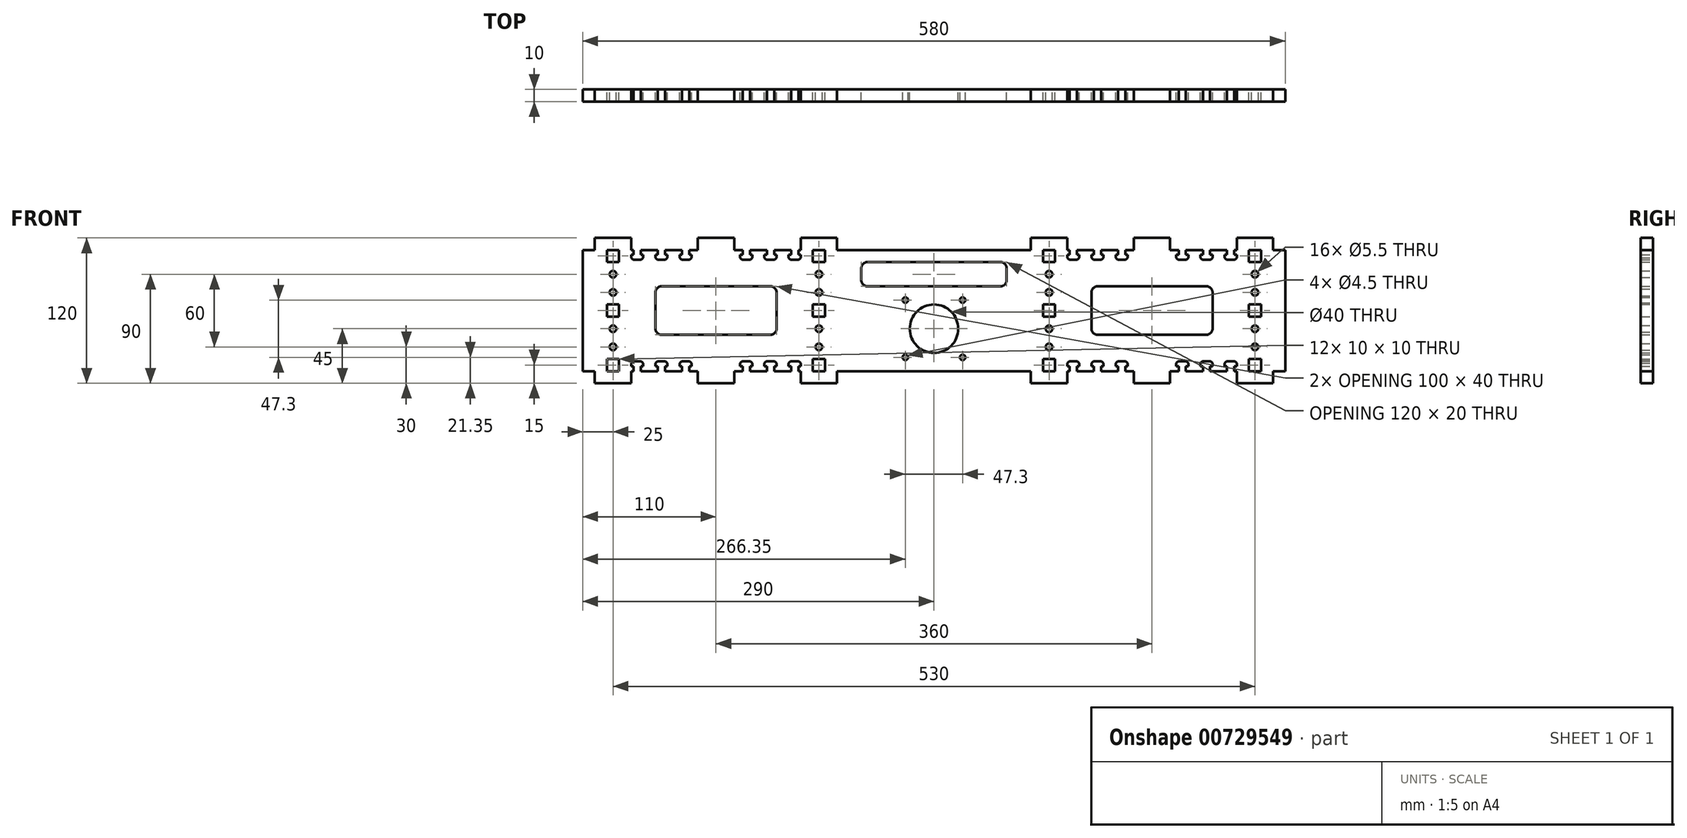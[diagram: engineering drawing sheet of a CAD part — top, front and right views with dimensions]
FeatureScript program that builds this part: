
annotation { "Feature Type Name" : "Feature", "Feature Type Description" : "" }
export const myFeature = defineFeature(function(context is Context, id is Id, definition is map)
    precondition{}
    {
        {
            var Q0;
            Q0=qCreatedBy(makeId("Front.planeOp"),FACE);
            var sketch = newSketch(context, id + "F0", { "sketchPlane" : qUnion([Q0])});
            skLineSegment(sketch, "E0.bottom", {"start": v(0, -50) * mm, "end": v(-290, -50) * mm, "construction": true});
            skLineSegment(sketch, "E0.top", {"start": v(0, 50) * mm, "end": v(-165, 50) * mm, "construction": true});
            skLineSegment(sketch, "E0.right", {"start": v(-290, -50) * mm, "end": v(-290, 50) * mm});
            skLineSegment(sketch, "E1", {"start": v(0, -50) * mm, "end": v(0, 83) * mm, "construction": true});
            skLineSegment(sketch, "E2", {"start": v(-265, 50) * mm, "end": v(-265, -50) * mm, "construction": true});
            skPoint(sketch, "E3.middle", {"position": v(-265, 0) * mm});
            skLineSegment(sketch, "E4.bottom", {"start": v(-260, 40) * mm, "end": v(-270, 40) * mm});
            skLineSegment(sketch, "E4.top", {"start": v(-260, 50) * mm, "end": v(-270, 50) * mm});
            skLineSegment(sketch, "E4.left", {"start": v(-260, 40) * mm, "end": v(-260, 50) * mm});
            skLineSegment(sketch, "E4.right", {"start": v(-270, 40) * mm, "end": v(-270, 50) * mm});
            skPoint(sketch, "E4.middle", {"position": v(-265, 45) * mm});
            skLineSegment(sketch, "E5", {"start": v(0, 0) * mm, "end": v(-290, 0) * mm, "construction": true});
            skLineSegment(sketch, "E6.bottom", {"start": v(-260, 5) * mm, "end": v(-270, 5) * mm});
            skLineSegment(sketch, "E6.top", {"start": v(-260, -5) * mm, "end": v(-270, -5) * mm});
            skLineSegment(sketch, "E6.left", {"start": v(-260, 5) * mm, "end": v(-260, -5) * mm});
            skLineSegment(sketch, "E6.right", {"start": v(-270, 5) * mm, "end": v(-270, -5) * mm});
            skLineSegment(sketch, "E7", {"start": v(-180, 63.21) * mm, "end": v(-180, -50) * mm, "construction": true});
            skLineSegment(sketch, "E8.bottom", {"start": v(-195, 60) * mm, "end": v(-180, 60) * mm});
            skLineSegment(sketch, "E8.left", {"start": v(-195, 60) * mm, "end": v(-195, 50) * mm});
            skPoint(sketch, "E8.middle", {"position": v(-180, 50) * mm});
            skLineSegment(sketch, "E9.trimOffspring", {"start": v(-195, 50) * mm, "end": v(-290, 50) * mm, "construction": true});
            skLineSegment(sketch, "E10.MirrorCS", {"start": v(-165, 60) * mm, "end": v(-180, 60) * mm});
            skLineSegment(sketch, "E11.MirrorCS", {"start": v(-165, 60) * mm, "end": v(-165, 50) * mm});
            skLineSegment(sketch, "E12.MirrorCS", {"start": v(-260, -40) * mm, "end": v(-260, -50) * mm});
            skLineSegment(sketch, "E13.MirrorCS", {"start": v(-260, -50) * mm, "end": v(-270, -50) * mm});
            skLineSegment(sketch, "E14.MirrorCS", {"start": v(-270, -40) * mm, "end": v(-270, -50) * mm});
            skLineSegment(sketch, "E15.MirrorCS", {"start": v(-260, -40) * mm, "end": v(-270, -40) * mm});
            skLineSegment(sketch, "E16.MirrorCS", {"start": v(-100, 40) * mm, "end": v(-100, 50) * mm});
            skLineSegment(sketch, "E17.MirrorCS", {"start": v(-100, 50) * mm, "end": v(-90, 50) * mm});
            skLineSegment(sketch, "E18.MirrorCS", {"start": v(-90, 40) * mm, "end": v(-90, 50) * mm});
            skLineSegment(sketch, "E19.MirrorCS", {"start": v(-100, 40) * mm, "end": v(-90, 40) * mm});
            skLineSegment(sketch, "E20.MirrorCS", {"start": v(-100, 5) * mm, "end": v(-90, 5) * mm});
            skLineSegment(sketch, "E21.MirrorCS", {"start": v(-100, 5) * mm, "end": v(-100, -5) * mm});
            skLineSegment(sketch, "E22.MirrorCS", {"start": v(-90, 5) * mm, "end": v(-90, -5) * mm});
            skLineSegment(sketch, "E23.MirrorCS", {"start": v(-100, -5) * mm, "end": v(-90, -5) * mm});
            skLineSegment(sketch, "E24.MirrorCS", {"start": v(-195, -60) * mm, "end": v(-195, -50) * mm});
            skLineSegment(sketch, "E25.MirrorCS", {"start": v(-195, -60) * mm, "end": v(-180, -60) * mm});
            skLineSegment(sketch, "E26.MirrorCS", {"start": v(-165, -60) * mm, "end": v(-180, -60) * mm});
            skLineSegment(sketch, "E27.MirrorCS", {"start": v(-165, -60) * mm, "end": v(-165, -50) * mm});
            skLineSegment(sketch, "E28.MirrorCS", {"start": v(0, -50) * mm, "end": v(-165, -50) * mm, "construction": true});
            skLineSegment(sketch, "E29.MirrorCS", {"start": v(-90, -40) * mm, "end": v(-90, -50) * mm});
            skLineSegment(sketch, "E30.MirrorCS", {"start": v(-100, -40) * mm, "end": v(-90, -40) * mm});
            skLineSegment(sketch, "E31.MirrorCS", {"start": v(-100, -50) * mm, "end": v(-90, -50) * mm});
            skLineSegment(sketch, "E32.MirrorCS", {"start": v(-100, -40) * mm, "end": v(-100, -50) * mm});
            skLineSegment(sketch, "E33", {"start": v(-290, 50) * mm, "end": v(-280, 50) * mm});
            skLineSegment(sketch, "E34", {"start": v(-280, 50) * mm, "end": v(-280, 60) * mm});
            skLineSegment(sketch, "E35", {"start": v(-280, 60) * mm, "end": v(-250, 60) * mm});
            skLineSegment(sketch, "E36", {"start": v(-250, 60) * mm, "end": v(-250, 50) * mm});
            skLineSegment(sketch, "E37.MirrorCS", {"start": v(-250, -60) * mm, "end": v(-250, -50) * mm});
            skLineSegment(sketch, "E38.MirrorCS", {"start": v(-280, -60) * mm, "end": v(-250, -60) * mm});
            skLineSegment(sketch, "E39.MirrorCS", {"start": v(-290, -50) * mm, "end": v(-280, -50) * mm});
            skLineSegment(sketch, "E40.MirrorCS", {"start": v(-280, -50) * mm, "end": v(-280, -60) * mm});
            skLineSegment(sketch, "E41.MirrorCS", {"start": v(-195, -50) * mm, "end": v(-290, -50) * mm, "construction": true});
            skLineSegment(sketch, "E42", {"start": v(-205, 42) * mm, "end": v(-205, 50) * mm, "construction": true});
            skLineSegment(sketch, "E43", {"start": v(-205, 42) * mm, "end": v(-201.6, 42) * mm});
            skLineSegment(sketch, "E44", {"start": v(-201.6, 42) * mm, "end": v(-200, 43.6) * mm});
            skLineSegment(sketch, "E45", {"start": v(-200, 43.6) * mm, "end": v(-200, 46) * mm});
            skLineSegment(sketch, "E46", {"start": v(-200, 46) * mm, "end": v(-202, 46) * mm});
            skLineSegment(sketch, "E47", {"start": v(-202, 46) * mm, "end": v(-202, 50) * mm});
            skLineSegment(sketch, "E48", {"start": v(-202, 50) * mm, "end": v(-208, 50) * mm, "construction": true});
            skLineSegment(sketch, "E49", {"start": v(-207.5, 42) * mm, "end": v(-207.5, 50) * mm, "construction": true});
            skLineSegment(sketch, "E50.MirrorCS", {"start": v(-205, 42) * mm, "end": v(-208.4, 42) * mm});
            skLineSegment(sketch, "E51.MirrorCS", {"start": v(-202.5, 42) * mm, "end": v(-202.5, 50) * mm, "construction": true});
            skLineSegment(sketch, "E52.MirrorCS", {"start": v(-208, 50) * mm, "end": v(-202, 50) * mm, "construction": true});
            skLineSegment(sketch, "E53.MirrorCS", {"start": v(-208, 46) * mm, "end": v(-208, 50) * mm});
            skLineSegment(sketch, "E54.MirrorCS", {"start": v(-210, 46) * mm, "end": v(-208, 46) * mm});
            skLineSegment(sketch, "E55.MirrorCS", {"start": v(-210, 43.6) * mm, "end": v(-210, 46) * mm});
            skLineSegment(sketch, "E56.MirrorCS", {"start": v(-208.4, 42) * mm, "end": v(-210, 43.6) * mm});
            skLineSegment(sketch, "E57.1.0.0", {"start": v(-221.6, 42) * mm, "end": v(-220, 43.6) * mm});
            skLineSegment(sketch, "E57.1.0.1", {"start": v(-220, 46) * mm, "end": v(-222, 46) * mm});
            skLineSegment(sketch, "E57.1.0.2", {"start": v(-225, 42) * mm, "end": v(-221.6, 42) * mm});
            skLineSegment(sketch, "E57.1.0.3", {"start": v(-228, 46) * mm, "end": v(-228, 50) * mm});
            skLineSegment(sketch, "E57.1.0.4", {"start": v(-230, 46) * mm, "end": v(-228, 46) * mm});
            skLineSegment(sketch, "E57.1.0.5", {"start": v(-225, 42) * mm, "end": v(-228.4, 42) * mm});
            skLineSegment(sketch, "E57.1.0.6", {"start": v(-230, 43.6) * mm, "end": v(-230, 46) * mm});
            skLineSegment(sketch, "E57.1.0.7", {"start": v(-220, 43.6) * mm, "end": v(-220, 46) * mm});
            skLineSegment(sketch, "E57.1.0.8", {"start": v(-228.4, 42) * mm, "end": v(-230, 43.6) * mm});
            skLineSegment(sketch, "E57.1.0.9", {"start": v(-222, 46) * mm, "end": v(-222, 50) * mm});
            skLineSegment(sketch, "E57.1.0.10", {"start": v(-222, 50) * mm, "end": v(-228, 50) * mm, "construction": true});
            skLineSegment(sketch, "E57.2.0.0", {"start": v(-241.6, 42) * mm, "end": v(-240, 43.6) * mm});
            skLineSegment(sketch, "E57.2.0.1", {"start": v(-240, 46) * mm, "end": v(-242, 46) * mm});
            skLineSegment(sketch, "E57.2.0.2", {"start": v(-245, 42) * mm, "end": v(-241.6, 42) * mm});
            skLineSegment(sketch, "E57.2.0.3", {"start": v(-248, 46) * mm, "end": v(-248, 50) * mm});
            skLineSegment(sketch, "E57.2.0.4", {"start": v(-250, 46) * mm, "end": v(-248, 46) * mm});
            skLineSegment(sketch, "E57.2.0.5", {"start": v(-245, 42) * mm, "end": v(-248.4, 42) * mm});
            skLineSegment(sketch, "E57.2.0.6", {"start": v(-250, 43.6) * mm, "end": v(-250, 46) * mm});
            skLineSegment(sketch, "E57.2.0.7", {"start": v(-240, 43.6) * mm, "end": v(-240, 46) * mm});
            skLineSegment(sketch, "E57.2.0.8", {"start": v(-248.4, 42) * mm, "end": v(-250, 43.6) * mm});
            skLineSegment(sketch, "E57.2.0.9", {"start": v(-242, 46) * mm, "end": v(-242, 50) * mm});
            skLineSegment(sketch, "E57.2.0.10", {"start": v(-242, 50) * mm, "end": v(-248, 50) * mm, "construction": true});
            skLineSegment(sketch, "E57.direction1", {"start": v(-208.4, 42) * mm, "end": v(-228.4, 42) * mm, "construction": true});
            skLineSegment(sketch, "E58", {"start": v(-250, 50) * mm, "end": v(-248, 50) * mm});
            skLineSegment(sketch, "E59", {"start": v(-242, 50) * mm, "end": v(-228, 50) * mm});
            skLineSegment(sketch, "E60", {"start": v(-222, 50) * mm, "end": v(-208, 50) * mm});
            skLineSegment(sketch, "E61", {"start": v(-195, 50) * mm, "end": v(-202, 50) * mm});
            skLineSegment(sketch, "E62.MirrorCS", {"start": v(-110, 50) * mm, "end": v(-112, 50) * mm});
            skLineSegment(sketch, "E63.MirrorCS", {"start": v(-152, 50) * mm, "end": v(-158, 50) * mm, "construction": true});
            skLineSegment(sketch, "E64.MirrorCS", {"start": v(-138, 50) * mm, "end": v(-132, 50) * mm, "construction": true});
            skLineSegment(sketch, "E65.MirrorCS", {"start": v(-165, 50) * mm, "end": v(-158, 50) * mm});
            skLineSegment(sketch, "E66.MirrorCS", {"start": v(-70, 50) * mm, "end": v(-80, 50) * mm});
            skLineSegment(sketch, "E67.MirrorCS", {"start": v(-158, 50) * mm, "end": v(-152, 50) * mm, "construction": true});
            skLineSegment(sketch, "E68.MirrorCS", {"start": v(-118, 50) * mm, "end": v(-112, 50) * mm, "construction": true});
            skLineSegment(sketch, "E69.MirrorCS", {"start": v(-118, 50) * mm, "end": v(-132, 50) * mm});
            skLineSegment(sketch, "E70.MirrorCS", {"start": v(-138, 50) * mm, "end": v(-152, 50) * mm});
            skLineSegment(sketch, "E71.MirrorCS", {"start": v(-80, 60) * mm, "end": v(-110, 60) * mm});
            skLineSegment(sketch, "E72.MirrorCS", {"start": v(-80, 50) * mm, "end": v(-80, 60) * mm});
            skLineSegment(sketch, "E73.MirrorCS", {"start": v(-110, 60) * mm, "end": v(-110, 50) * mm});
            skLineSegment(sketch, "E74.MirrorCS", {"start": v(-165, 50) * mm, "end": v(-70, 50) * mm, "construction": true});
            skLineSegment(sketch, "E75.MirrorCS", {"start": v(-155, 42) * mm, "end": v(-151.6, 42) * mm});
            skLineSegment(sketch, "E76.MirrorCS", {"start": v(-158, 46) * mm, "end": v(-158, 50) * mm});
            skLineSegment(sketch, "E77.MirrorCS", {"start": v(-158.4, 42) * mm, "end": v(-160, 43.6) * mm});
            skLineSegment(sketch, "E78.MirrorCS", {"start": v(-160, 46) * mm, "end": v(-158, 46) * mm});
            skLineSegment(sketch, "E79.MirrorCS", {"start": v(-131.6, 42) * mm, "end": v(-130, 43.6) * mm});
            skLineSegment(sketch, "E80.MirrorCS", {"start": v(-160, 43.6) * mm, "end": v(-160, 46) * mm});
            skLineSegment(sketch, "E81.MirrorCS", {"start": v(-112, 46) * mm, "end": v(-112, 50) * mm});
            skLineSegment(sketch, "E82.MirrorCS", {"start": v(-151.6, 42) * mm, "end": v(-150, 43.6) * mm});
            skLineSegment(sketch, "E83.MirrorCS", {"start": v(-155, 42) * mm, "end": v(-158.4, 42) * mm});
            skLineSegment(sketch, "E84.MirrorCS", {"start": v(-157.5, 42) * mm, "end": v(-157.5, 50) * mm, "construction": true});
            skLineSegment(sketch, "E85.MirrorCS", {"start": v(-110, 46) * mm, "end": v(-112, 46) * mm});
            skLineSegment(sketch, "E86.MirrorCS", {"start": v(-111.6, 42) * mm, "end": v(-110, 43.6) * mm});
            skLineSegment(sketch, "E87.MirrorCS", {"start": v(-132, 46) * mm, "end": v(-132, 50) * mm});
            skLineSegment(sketch, "E88.MirrorCS", {"start": v(-130, 43.6) * mm, "end": v(-130, 46) * mm});
            skLineSegment(sketch, "E89.MirrorCS", {"start": v(-140, 46) * mm, "end": v(-138, 46) * mm});
            skLineSegment(sketch, "E90.MirrorCS", {"start": v(-138.4, 42) * mm, "end": v(-140, 43.6) * mm});
            skLineSegment(sketch, "E91.MirrorCS", {"start": v(-152.5, 42) * mm, "end": v(-152.5, 50) * mm, "construction": true});
            skLineSegment(sketch, "E92.MirrorCS", {"start": v(-138, 46) * mm, "end": v(-138, 50) * mm});
            skLineSegment(sketch, "E93.MirrorCS", {"start": v(-118.4, 42) * mm, "end": v(-120, 43.6) * mm});
            skLineSegment(sketch, "E94.MirrorCS", {"start": v(-120, 43.6) * mm, "end": v(-120, 46) * mm});
            skLineSegment(sketch, "E95.MirrorCS", {"start": v(-150, 46) * mm, "end": v(-152, 46) * mm});
            skLineSegment(sketch, "E96.MirrorCS", {"start": v(-135, 42) * mm, "end": v(-138.4, 42) * mm});
            skLineSegment(sketch, "E97.MirrorCS", {"start": v(-150, 43.6) * mm, "end": v(-150, 46) * mm});
            skLineSegment(sketch, "E98.MirrorCS", {"start": v(-120, 46) * mm, "end": v(-118, 46) * mm});
            skLineSegment(sketch, "E99.MirrorCS", {"start": v(-115, 42) * mm, "end": v(-111.6, 42) * mm});
            skLineSegment(sketch, "E100.MirrorCS", {"start": v(-130, 46) * mm, "end": v(-132, 46) * mm});
            skLineSegment(sketch, "E101.MirrorCS", {"start": v(-118, 46) * mm, "end": v(-118, 50) * mm});
            skLineSegment(sketch, "E102.MirrorCS", {"start": v(-110, 43.6) * mm, "end": v(-110, 46) * mm});
            skLineSegment(sketch, "E103.MirrorCS", {"start": v(-115, 42) * mm, "end": v(-118.4, 42) * mm});
            skLineSegment(sketch, "E104.MirrorCS", {"start": v(-140, 43.6) * mm, "end": v(-140, 46) * mm});
            skLineSegment(sketch, "E105.MirrorCS", {"start": v(-152, 46) * mm, "end": v(-152, 50) * mm});
            skLineSegment(sketch, "E106.MirrorCS", {"start": v(-135, 42) * mm, "end": v(-131.6, 42) * mm});
            skLineSegment(sketch, "E107.MirrorCS", {"start": v(-155, 42) * mm, "end": v(-155, 50) * mm, "construction": true});
            skLineSegment(sketch, "E108.MirrorCS", {"start": v(-151.6, 42) * mm, "end": v(-131.6, 42) * mm, "construction": true});
            skLineSegment(sketch, "E109", {"start": v(-70, 50) * mm, "end": v(0, 50) * mm});
            skLineSegment(sketch, "E110.MirrorCS", {"start": v(-208, -50) * mm, "end": v(-202, -50) * mm, "construction": true});
            skLineSegment(sketch, "E111.MirrorCS", {"start": v(-152, -50) * mm, "end": v(-158, -50) * mm, "construction": true});
            skLineSegment(sketch, "E112.MirrorCS", {"start": v(-202, -50) * mm, "end": v(-208, -50) * mm, "construction": true});
            skLineSegment(sketch, "E113.MirrorCS", {"start": v(-202, -46) * mm, "end": v(-202, -50) * mm});
            skLineSegment(sketch, "E114.MirrorCS", {"start": v(-205, -42) * mm, "end": v(-201.6, -42) * mm});
            skLineSegment(sketch, "E115.MirrorCS", {"start": v(-201.6, -42) * mm, "end": v(-200, -43.6) * mm});
            skLineSegment(sketch, "E116.MirrorCS", {"start": v(-208.4, -42) * mm, "end": v(-210, -43.6) * mm});
            skLineSegment(sketch, "E117.MirrorCS", {"start": v(-151.6, -42) * mm, "end": v(-150, -43.6) * mm});
            skLineSegment(sketch, "E118.MirrorCS", {"start": v(-208, -46) * mm, "end": v(-208, -50) * mm});
            skLineSegment(sketch, "E119.MirrorCS", {"start": v(-158, -50) * mm, "end": v(-152, -50) * mm, "construction": true});
            skLineSegment(sketch, "E120.MirrorCS", {"start": v(-200, -46) * mm, "end": v(-202, -46) * mm});
            skLineSegment(sketch, "E121.MirrorCS", {"start": v(-158, -46) * mm, "end": v(-158, -50) * mm});
            skLineSegment(sketch, "E122.MirrorCS", {"start": v(-165, -50) * mm, "end": v(-158, -50) * mm});
            skLineSegment(sketch, "E123.MirrorCS", {"start": v(-200, -43.6) * mm, "end": v(-200, -46) * mm});
            skLineSegment(sketch, "E124.MirrorCS", {"start": v(-155, -42) * mm, "end": v(-151.6, -42) * mm});
            skLineSegment(sketch, "E125.MirrorCS", {"start": v(-202.5, -42) * mm, "end": v(-202.5, -50) * mm, "construction": true});
            skLineSegment(sketch, "E126.MirrorCS", {"start": v(-205, -42) * mm, "end": v(-208.4, -42) * mm});
            skLineSegment(sketch, "E127.MirrorCS", {"start": v(-138, -50) * mm, "end": v(-132, -50) * mm, "construction": true});
            skLineSegment(sketch, "E128.MirrorCS", {"start": v(-222, -46) * mm, "end": v(-222, -50) * mm});
            skLineSegment(sketch, "E129.MirrorCS", {"start": v(-155, -42) * mm, "end": v(-158.4, -42) * mm});
            skLineSegment(sketch, "E130.MirrorCS", {"start": v(-160, -43.6) * mm, "end": v(-160, -46) * mm});
            skLineSegment(sketch, "E131.MirrorCS", {"start": v(-150, -43.6) * mm, "end": v(-150, -46) * mm});
            skLineSegment(sketch, "E132.MirrorCS", {"start": v(-115, -42) * mm, "end": v(-111.6, -42) * mm});
            skLineSegment(sketch, "E133.MirrorCS", {"start": v(-242, -50) * mm, "end": v(-248, -50) * mm, "construction": true});
            skLineSegment(sketch, "E134.MirrorCS", {"start": v(-250, -43.6) * mm, "end": v(-250, -46) * mm});
            skLineSegment(sketch, "E135.MirrorCS", {"start": v(-138, -46) * mm, "end": v(-138, -50) * mm});
            skLineSegment(sketch, "E136.MirrorCS", {"start": v(-207.5, -42) * mm, "end": v(-207.5, -50) * mm, "construction": true});
            skLineSegment(sketch, "E137.MirrorCS", {"start": v(-130, -43.6) * mm, "end": v(-130, -46) * mm});
            skLineSegment(sketch, "E138.MirrorCS", {"start": v(-220, -46) * mm, "end": v(-222, -46) * mm});
            skLineSegment(sketch, "E139.MirrorCS", {"start": v(-135, -42) * mm, "end": v(-131.6, -42) * mm});
            skLineSegment(sketch, "E140.MirrorCS", {"start": v(-225, -42) * mm, "end": v(-228.4, -42) * mm});
            skLineSegment(sketch, "E141.MirrorCS", {"start": v(-228.4, -42) * mm, "end": v(-230, -43.6) * mm});
            skLineSegment(sketch, "E142.MirrorCS", {"start": v(-152, -46) * mm, "end": v(-152, -50) * mm});
            skLineSegment(sketch, "E143.MirrorCS", {"start": v(-118, -50) * mm, "end": v(-112, -50) * mm, "construction": true});
            skLineSegment(sketch, "E144.MirrorCS", {"start": v(-205, -42) * mm, "end": v(-205, -50) * mm, "construction": true});
            skLineSegment(sketch, "E145.MirrorCS", {"start": v(-210, -46) * mm, "end": v(-208, -46) * mm});
            skLineSegment(sketch, "E146.MirrorCS", {"start": v(-222, -50) * mm, "end": v(-228, -50) * mm, "construction": true});
            skLineSegment(sketch, "E147.MirrorCS", {"start": v(-110, -50) * mm, "end": v(-112, -50) * mm});
            skLineSegment(sketch, "E148.MirrorCS", {"start": v(-110, -43.6) * mm, "end": v(-110, -46) * mm});
            skLineSegment(sketch, "E149.MirrorCS", {"start": v(-112, -46) * mm, "end": v(-112, -50) * mm});
            skLineSegment(sketch, "E150.MirrorCS", {"start": v(-250, -50) * mm, "end": v(-248, -50) * mm});
            skLineSegment(sketch, "E151.MirrorCS", {"start": v(-131.6, -42) * mm, "end": v(-130, -43.6) * mm});
            skLineSegment(sketch, "E152.MirrorCS", {"start": v(-248, -46) * mm, "end": v(-248, -50) * mm});
            skLineSegment(sketch, "E153.MirrorCS", {"start": v(-115, -42) * mm, "end": v(-118.4, -42) * mm});
            skLineSegment(sketch, "E154.MirrorCS", {"start": v(-160, -46) * mm, "end": v(-158, -46) * mm});
            skLineSegment(sketch, "E155.MirrorCS", {"start": v(-250, -46) * mm, "end": v(-248, -46) * mm});
            skLineSegment(sketch, "E156.MirrorCS", {"start": v(-230, -43.6) * mm, "end": v(-230, -46) * mm});
            skLineSegment(sketch, "E157.MirrorCS", {"start": v(-110, -46) * mm, "end": v(-112, -46) * mm});
            skLineSegment(sketch, "E158.MirrorCS", {"start": v(-195, -50) * mm, "end": v(-202, -50) * mm});
            skLineSegment(sketch, "E159.MirrorCS", {"start": v(-220, -43.6) * mm, "end": v(-220, -46) * mm});
            skLineSegment(sketch, "E160.MirrorCS", {"start": v(-210, -43.6) * mm, "end": v(-210, -46) * mm});
            skLineSegment(sketch, "E161.MirrorCS", {"start": v(-140, -46) * mm, "end": v(-138, -46) * mm});
            skLineSegment(sketch, "E162.MirrorCS", {"start": v(-248.4, -42) * mm, "end": v(-250, -43.6) * mm});
            skLineSegment(sketch, "E163.MirrorCS", {"start": v(-157.5, -42) * mm, "end": v(-157.5, -50) * mm, "construction": true});
            skLineSegment(sketch, "E164.MirrorCS", {"start": v(-155, -42) * mm, "end": v(-155, -50) * mm, "construction": true});
            skLineSegment(sketch, "E165.MirrorCS", {"start": v(-240, -46) * mm, "end": v(-242, -46) * mm});
            skLineSegment(sketch, "E166.MirrorCS", {"start": v(-120, -46) * mm, "end": v(-118, -46) * mm});
            skLineSegment(sketch, "E167.MirrorCS", {"start": v(-158.4, -42) * mm, "end": v(-160, -43.6) * mm});
            skLineSegment(sketch, "E168.MirrorCS", {"start": v(-230, -46) * mm, "end": v(-228, -46) * mm});
            skLineSegment(sketch, "E169.MirrorCS", {"start": v(-225, -42) * mm, "end": v(-221.6, -42) * mm});
            skLineSegment(sketch, "E170.MirrorCS", {"start": v(-118, -46) * mm, "end": v(-118, -50) * mm});
            skLineSegment(sketch, "E171.MirrorCS", {"start": v(-118.4, -42) * mm, "end": v(-120, -43.6) * mm});
            skLineSegment(sketch, "E172.MirrorCS", {"start": v(-130, -46) * mm, "end": v(-132, -46) * mm});
            skLineSegment(sketch, "E173.MirrorCS", {"start": v(-118, -50) * mm, "end": v(-132, -50) * mm});
            skLineSegment(sketch, "E174.MirrorCS", {"start": v(-70, -50) * mm, "end": v(-80, -50) * mm});
            skLineSegment(sketch, "E175.MirrorCS", {"start": v(-221.6, -42) * mm, "end": v(-220, -43.6) * mm});
            skLineSegment(sketch, "E176.MirrorCS", {"start": v(-132, -46) * mm, "end": v(-132, -50) * mm});
            skLineSegment(sketch, "E177.MirrorCS", {"start": v(-150, -46) * mm, "end": v(-152, -46) * mm});
            skLineSegment(sketch, "E178.MirrorCS", {"start": v(-138.4, -42) * mm, "end": v(-140, -43.6) * mm});
            skLineSegment(sketch, "E179.MirrorCS", {"start": v(-228, -46) * mm, "end": v(-228, -50) * mm});
            skLineSegment(sketch, "E180.MirrorCS", {"start": v(-245, -42) * mm, "end": v(-241.6, -42) * mm});
            skLineSegment(sketch, "E181.MirrorCS", {"start": v(-138, -50) * mm, "end": v(-152, -50) * mm});
            skLineSegment(sketch, "E182.MirrorCS", {"start": v(-111.6, -42) * mm, "end": v(-110, -43.6) * mm});
            skLineSegment(sketch, "E183.MirrorCS", {"start": v(-241.6, -42) * mm, "end": v(-240, -43.6) * mm});
            skLineSegment(sketch, "E184.MirrorCS", {"start": v(-120, -43.6) * mm, "end": v(-120, -46) * mm});
            skLineSegment(sketch, "E185.MirrorCS", {"start": v(-240, -43.6) * mm, "end": v(-240, -46) * mm});
            skLineSegment(sketch, "E186.MirrorCS", {"start": v(-135, -42) * mm, "end": v(-138.4, -42) * mm});
            skLineSegment(sketch, "E187.MirrorCS", {"start": v(-242, -46) * mm, "end": v(-242, -50) * mm});
            skLineSegment(sketch, "E188.MirrorCS", {"start": v(-152.5, -42) * mm, "end": v(-152.5, -50) * mm, "construction": true});
            skLineSegment(sketch, "E189.MirrorCS", {"start": v(-245, -42) * mm, "end": v(-248.4, -42) * mm});
            skLineSegment(sketch, "E190.MirrorCS", {"start": v(-140, -43.6) * mm, "end": v(-140, -46) * mm});
            skLineSegment(sketch, "E191.MirrorCS", {"start": v(-165, -50) * mm, "end": v(-70, -50) * mm, "construction": true});
            skLineSegment(sketch, "E192.MirrorCS", {"start": v(-242, -50) * mm, "end": v(-228, -50) * mm});
            skPoint(sketch, "E193.MirrorP", {"position": v(-180, -50) * mm});
            skLineSegment(sketch, "E194.MirrorCS", {"start": v(-70, -50) * mm, "end": v(0, -50) * mm});
            skLineSegment(sketch, "E195.MirrorCS", {"start": v(-222, -50) * mm, "end": v(-208, -50) * mm});
            skLineSegment(sketch, "E196.MirrorCS", {"start": v(-80, -50) * mm, "end": v(-80, -60) * mm});
            skLineSegment(sketch, "E197.MirrorCS", {"start": v(-208.4, -42) * mm, "end": v(-228.4, -42) * mm, "construction": true});
            skLineSegment(sketch, "E198.MirrorCS", {"start": v(-110, -60) * mm, "end": v(-110, -50) * mm});
            skLineSegment(sketch, "E199.MirrorCS", {"start": v(-151.6, -42) * mm, "end": v(-131.6, -42) * mm, "construction": true});
            skLineSegment(sketch, "E200.MirrorCS", {"start": v(-80, -60) * mm, "end": v(-110, -60) * mm});
            skPoint(sketch, "E201.MirrorP", {"position": v(-265, -45) * mm});
            skPoint(sketch, "E202.middle", {"position": v(0, -15) * mm});
            skCircle(sketch, "E203", {"center": v(0, -15) * mm, "radius": 20 * mm});
            skLineSegment(sketch, "E204.bottom", {"start": v(-23.65, 8.65) * mm, "end": v(23.65, 8.65) * mm, "construction": true});
            skLineSegment(sketch, "E204.top", {"start": v(-23.65, -38.65) * mm, "end": v(23.65, -38.65) * mm, "construction": true});
            skLineSegment(sketch, "E204.left", {"start": v(-23.65, 8.65) * mm, "end": v(-23.65, -38.65) * mm, "construction": true});
            skLineSegment(sketch, "E204.right", {"start": v(23.65, 8.65) * mm, "end": v(23.65, -38.65) * mm, "construction": true});
            skCircle(sketch, "E205", {"center": v(-23.65, 8.65) * mm, "radius": 2.25 * mm});
            skCircle(sketch, "E206", {"center": v(23.65, 8.65) * mm, "radius": 2.25 * mm});
            skCircle(sketch, "E207", {"center": v(-23.65, -38.65) * mm, "radius": 2.25 * mm});
            skCircle(sketch, "E208", {"center": v(23.65, -38.65) * mm, "radius": 2.25 * mm});
            skLineSegment(sketch, "E209.MirrorCS", {"start": v(202, -50) * mm, "end": v(208, -50) * mm, "construction": true});
            skLineSegment(sketch, "E210.MirrorCS", {"start": v(152, 50) * mm, "end": v(158, 50) * mm, "construction": true});
            skLineSegment(sketch, "E211.MirrorCS", {"start": v(158, 50) * mm, "end": v(152, 50) * mm, "construction": true});
            skLineSegment(sketch, "E212.MirrorCS", {"start": v(152, 46) * mm, "end": v(152, 50) * mm});
            skLineSegment(sketch, "E213.MirrorCS", {"start": v(202, 46) * mm, "end": v(202, 50) * mm});
            skLineSegment(sketch, "E214.MirrorCS", {"start": v(208, 50) * mm, "end": v(202, 50) * mm, "construction": true});
            skLineSegment(sketch, "E215.MirrorCS", {"start": v(208, -50) * mm, "end": v(202, -50) * mm, "construction": true});
            skLineSegment(sketch, "E216.MirrorCS", {"start": v(207.5, 42) * mm, "end": v(207.5, 50) * mm, "construction": true});
            skLineSegment(sketch, "E217.MirrorCS", {"start": v(165, -50) * mm, "end": v(158, -50) * mm});
            skLineSegment(sketch, "E218.MirrorCS", {"start": v(220, -46) * mm, "end": v(222, -46) * mm});
            skLineSegment(sketch, "E219.MirrorCS", {"start": v(205, 42) * mm, "end": v(205, 50) * mm, "construction": true});
            skLineSegment(sketch, "E220.MirrorCS", {"start": v(155, 42) * mm, "end": v(158.4, 42) * mm});
            skLineSegment(sketch, "E221.MirrorCS", {"start": v(220, 46) * mm, "end": v(222, 46) * mm});
            skLineSegment(sketch, "E222.MirrorCS", {"start": v(205, 42) * mm, "end": v(208.4, 42) * mm});
            skLineSegment(sketch, "E223.MirrorCS", {"start": v(155, 42) * mm, "end": v(155, 50) * mm, "construction": true});
            skLineSegment(sketch, "E224.MirrorCS", {"start": v(152.5, 42) * mm, "end": v(152.5, 50) * mm, "construction": true});
            skLineSegment(sketch, "E225.MirrorCS", {"start": v(155, 42) * mm, "end": v(151.6, 42) * mm});
            skLineSegment(sketch, "E226.MirrorCS", {"start": v(205, 42) * mm, "end": v(201.6, 42) * mm});
            skLineSegment(sketch, "E227.MirrorCS", {"start": v(157.5, 42) * mm, "end": v(157.5, 50) * mm, "construction": true});
            skLineSegment(sketch, "E228.MirrorCS", {"start": v(165, 50) * mm, "end": v(158, 50) * mm});
            skLineSegment(sketch, "E229.MirrorCS", {"start": v(202, 50) * mm, "end": v(208, 50) * mm, "construction": true});
            skLineSegment(sketch, "E230.MirrorCS", {"start": v(202.5, 42) * mm, "end": v(202.5, 50) * mm, "construction": true});
            skLineSegment(sketch, "E231.MirrorCS", {"start": v(158, 46) * mm, "end": v(158, 50) * mm});
            skLineSegment(sketch, "E232.MirrorCS", {"start": v(208, 46) * mm, "end": v(208, 50) * mm});
            skLineSegment(sketch, "E233.MirrorCS", {"start": v(150, 46) * mm, "end": v(152, 46) * mm});
            skLineSegment(sketch, "E234.MirrorCS", {"start": v(195, -50) * mm, "end": v(202, -50) * mm});
            skLineSegment(sketch, "E235.MirrorCS", {"start": v(208, -46) * mm, "end": v(208, -50) * mm});
            skLineSegment(sketch, "E236.MirrorCS", {"start": v(152, -50) * mm, "end": v(158, -50) * mm, "construction": true});
            skLineSegment(sketch, "E237.MirrorCS", {"start": v(160, -46) * mm, "end": v(158, -46) * mm});
            skLineSegment(sketch, "E238.MirrorCS", {"start": v(150, -43.6) * mm, "end": v(150, -46) * mm});
            skLineSegment(sketch, "E239.MirrorCS", {"start": v(157.5, -42) * mm, "end": v(157.5, -50) * mm, "construction": true});
            skLineSegment(sketch, "E240.MirrorCS", {"start": v(222, 46) * mm, "end": v(222, 50) * mm});
            skLineSegment(sketch, "E241.MirrorCS", {"start": v(250, -46) * mm, "end": v(248, -46) * mm});
            skLineSegment(sketch, "E242.MirrorCS", {"start": v(210, 43.6) * mm, "end": v(210, 46) * mm});
            skLineSegment(sketch, "E243.MirrorCS", {"start": v(205, -42) * mm, "end": v(205, -50) * mm, "construction": true});
            skLineSegment(sketch, "E244.MirrorCS", {"start": v(222, -46) * mm, "end": v(222, -50) * mm});
            skLineSegment(sketch, "E245.MirrorCS", {"start": v(208.4, -42) * mm, "end": v(210, -43.6) * mm});
            skLineSegment(sketch, "E246.MirrorCS", {"start": v(130, 46) * mm, "end": v(132, 46) * mm});
            skLineSegment(sketch, "E247.MirrorCS", {"start": v(132, -46) * mm, "end": v(132, -50) * mm});
            skLineSegment(sketch, "E248.MirrorCS", {"start": v(220, 43.6) * mm, "end": v(220, 46) * mm});
            skLineSegment(sketch, "E249.MirrorCS", {"start": v(210, -43.6) * mm, "end": v(210, -46) * mm});
            skLineSegment(sketch, "E250.MirrorCS", {"start": v(158, -46) * mm, "end": v(158, -50) * mm});
            skLineSegment(sketch, "E251.MirrorCS", {"start": v(155, -42) * mm, "end": v(155, -50) * mm, "construction": true});
            skLineSegment(sketch, "E252.MirrorCS", {"start": v(155, -42) * mm, "end": v(151.6, -42) * mm});
            skLineSegment(sketch, "E253.MirrorCS", {"start": v(152.5, -42) * mm, "end": v(152.5, -50) * mm, "construction": true});
            skLineSegment(sketch, "E254.MirrorCS", {"start": v(130, -46) * mm, "end": v(132, -46) * mm});
            skLineSegment(sketch, "E255.MirrorCS", {"start": v(201.6, 42) * mm, "end": v(200, 43.6) * mm});
            skLineSegment(sketch, "E256.MirrorCS", {"start": v(205, -42) * mm, "end": v(201.6, -42) * mm});
            skLineSegment(sketch, "E257.MirrorCS", {"start": v(130, -43.6) * mm, "end": v(130, -46) * mm});
            skLineSegment(sketch, "E258.MirrorCS", {"start": v(151.6, 42) * mm, "end": v(150, 43.6) * mm});
            skLineSegment(sketch, "E259.MirrorCS", {"start": v(152, -46) * mm, "end": v(152, -50) * mm});
            skLineSegment(sketch, "E260.MirrorCS", {"start": v(205, -42) * mm, "end": v(208.4, -42) * mm});
            skLineSegment(sketch, "E261.MirrorCS", {"start": v(221.6, -42) * mm, "end": v(220, -43.6) * mm});
            skLineSegment(sketch, "E262.MirrorCS", {"start": v(208.4, 42) * mm, "end": v(210, 43.6) * mm});
            skLineSegment(sketch, "E263.MirrorCS", {"start": v(220, -43.6) * mm, "end": v(220, -46) * mm});
            skLineSegment(sketch, "E264.MirrorCS", {"start": v(202.5, -42) * mm, "end": v(202.5, -50) * mm, "construction": true});
            skLineSegment(sketch, "E265.MirrorCS", {"start": v(210, -46) * mm, "end": v(208, -46) * mm});
            skLineSegment(sketch, "E266.MirrorCS", {"start": v(155, -42) * mm, "end": v(158.4, -42) * mm});
            skLineSegment(sketch, "E267.MirrorCS", {"start": v(221.6, 42) * mm, "end": v(220, 43.6) * mm});
            skLineSegment(sketch, "E268.MirrorCS", {"start": v(207.5, -42) * mm, "end": v(207.5, -50) * mm, "construction": true});
            skLineSegment(sketch, "E269.MirrorCS", {"start": v(150, 43.6) * mm, "end": v(150, 46) * mm});
            skLineSegment(sketch, "E270.MirrorCS", {"start": v(210, 46) * mm, "end": v(208, 46) * mm});
            skLineSegment(sketch, "E271.MirrorCS", {"start": v(200, 43.6) * mm, "end": v(200, 46) * mm});
            skLineSegment(sketch, "E272.MirrorCS", {"start": v(202, -46) * mm, "end": v(202, -50) * mm});
            skLineSegment(sketch, "E273.MirrorCS", {"start": v(158, -50) * mm, "end": v(152, -50) * mm, "construction": true});
            skLineSegment(sketch, "E274.MirrorCS", {"start": v(200, 46) * mm, "end": v(202, 46) * mm});
            skLineSegment(sketch, "E275.MirrorCS", {"start": v(228.4, 42) * mm, "end": v(230, 43.6) * mm});
            skLineSegment(sketch, "E276.MirrorCS", {"start": v(135, 42) * mm, "end": v(131.6, 42) * mm});
            skLineSegment(sketch, "E277.MirrorCS", {"start": v(138.4, 42) * mm, "end": v(140, 43.6) * mm});
            skLineSegment(sketch, "E278.MirrorCS", {"start": v(135, -42) * mm, "end": v(138.4, -42) * mm});
            skLineSegment(sketch, "E279.MirrorCS", {"start": v(118, -46) * mm, "end": v(118, -50) * mm});
            skLineSegment(sketch, "E280.MirrorCS", {"start": v(118, 50) * mm, "end": v(112, 50) * mm, "construction": true});
            skLineSegment(sketch, "E281.MirrorCS", {"start": v(250, 43.6) * mm, "end": v(250, 46) * mm});
            skLineSegment(sketch, "E282.MirrorCS", {"start": v(110, -50) * mm, "end": v(112, -50) * mm});
            skLineSegment(sketch, "E283.MirrorCS", {"start": v(201.6, -42) * mm, "end": v(200, -43.6) * mm});
            skLineSegment(sketch, "E284.MirrorCS", {"start": v(115, 42) * mm, "end": v(111.6, 42) * mm});
            skLineSegment(sketch, "E285.MirrorCS", {"start": v(70, -50) * mm, "end": v(0, -50) * mm});
            skLineSegment(sketch, "E286.MirrorCS", {"start": v(228, -46) * mm, "end": v(228, -50) * mm});
            skLineSegment(sketch, "E287.MirrorCS", {"start": v(200, -43.6) * mm, "end": v(200, -46) * mm});
            skLineSegment(sketch, "E288.MirrorCS", {"start": v(242, -46) * mm, "end": v(242, -50) * mm});
            skLineSegment(sketch, "E289.MirrorCS", {"start": v(118.4, -42) * mm, "end": v(120, -43.6) * mm});
            skLineSegment(sketch, "E290.MirrorCS", {"start": v(135, -42) * mm, "end": v(131.6, -42) * mm});
            skLineSegment(sketch, "E291.MirrorCS", {"start": v(290, -50) * mm, "end": v(280, -50) * mm});
            skLineSegment(sketch, "E292.MirrorCS", {"start": v(160, 43.6) * mm, "end": v(160, 46) * mm});
            skLineSegment(sketch, "E293.MirrorCS", {"start": v(248, 46) * mm, "end": v(248, 50) * mm});
            skLineSegment(sketch, "E294.MirrorCS", {"start": v(240, 43.6) * mm, "end": v(240, 46) * mm});
            skLineSegment(sketch, "E295.MirrorCS", {"start": v(225, 42) * mm, "end": v(221.6, 42) * mm});
            skLineSegment(sketch, "E296.MirrorCS", {"start": v(110, -43.6) * mm, "end": v(110, -46) * mm});
            skLineSegment(sketch, "E297.MirrorCS", {"start": v(135, 42) * mm, "end": v(138.4, 42) * mm});
            skLineSegment(sketch, "E298.MirrorCS", {"start": v(120, 46) * mm, "end": v(118, 46) * mm});
            skLineSegment(sketch, "E299.MirrorCS", {"start": v(245, -42) * mm, "end": v(241.6, -42) * mm});
            skLineSegment(sketch, "E300.MirrorCS", {"start": v(248.4, -42) * mm, "end": v(250, -43.6) * mm});
            skLineSegment(sketch, "E301.MirrorCS", {"start": v(250, 50) * mm, "end": v(248, 50) * mm});
            skLineSegment(sketch, "E302.MirrorCS", {"start": v(240, -43.6) * mm, "end": v(240, -46) * mm});
            skLineSegment(sketch, "E303.MirrorCS", {"start": v(225, -42) * mm, "end": v(221.6, -42) * mm});
            skLineSegment(sketch, "E304.MirrorCS", {"start": v(140, 46) * mm, "end": v(138, 46) * mm});
            skLineSegment(sketch, "E305.MirrorCS", {"start": v(195, 50) * mm, "end": v(202, 50) * mm});
            skLineSegment(sketch, "E306.MirrorCS", {"start": v(222, 50) * mm, "end": v(228, 50) * mm, "construction": true});
            skLineSegment(sketch, "E307.MirrorCS", {"start": v(138, 46) * mm, "end": v(138, 50) * mm});
            skLineSegment(sketch, "E308.MirrorCS", {"start": v(230, -43.6) * mm, "end": v(230, -46) * mm});
            skLineSegment(sketch, "E309.MirrorCS", {"start": v(225, -42) * mm, "end": v(228.4, -42) * mm});
            skLineSegment(sketch, "E310.MirrorCS", {"start": v(160, 46) * mm, "end": v(158, 46) * mm});
            skLineSegment(sketch, "E311.MirrorCS", {"start": v(110, 46) * mm, "end": v(112, 46) * mm});
            skLineSegment(sketch, "E312.MirrorCS", {"start": v(248.4, 42) * mm, "end": v(250, 43.6) * mm});
            skLineSegment(sketch, "E313.MirrorCS", {"start": v(240, 46) * mm, "end": v(242, 46) * mm});
            skLineSegment(sketch, "E314.MirrorCS", {"start": v(228, 46) * mm, "end": v(228, 50) * mm});
            skLineSegment(sketch, "E315.MirrorCS", {"start": v(112, -46) * mm, "end": v(112, -50) * mm});
            skLineSegment(sketch, "E316.MirrorCS", {"start": v(222, -50) * mm, "end": v(228, -50) * mm, "construction": true});
            skLineSegment(sketch, "E317.MirrorCS", {"start": v(132, 46) * mm, "end": v(132, 50) * mm});
            skLineSegment(sketch, "E318.MirrorCS", {"start": v(120, -43.6) * mm, "end": v(120, -46) * mm});
            skLineSegment(sketch, "E319.MirrorCS", {"start": v(230, 43.6) * mm, "end": v(230, 46) * mm});
            skLineSegment(sketch, "E320.MirrorCS", {"start": v(250, -50) * mm, "end": v(248, -50) * mm});
            skLineSegment(sketch, "E321.MirrorCS", {"start": v(160, -43.6) * mm, "end": v(160, -46) * mm});
            skLineSegment(sketch, "E322.MirrorCS", {"start": v(158.4, -42) * mm, "end": v(160, -43.6) * mm});
            skLineSegment(sketch, "E323.MirrorCS", {"start": v(250, -43.6) * mm, "end": v(250, -46) * mm});
            skLineSegment(sketch, "E324.MirrorCS", {"start": v(200, -46) * mm, "end": v(202, -46) * mm});
            skLineSegment(sketch, "E325.MirrorCS", {"start": v(151.6, -42) * mm, "end": v(150, -43.6) * mm});
            skLineSegment(sketch, "E326.MirrorCS", {"start": v(230, -46) * mm, "end": v(228, -46) * mm});
            skLineSegment(sketch, "E327.MirrorCS", {"start": v(140, 43.6) * mm, "end": v(140, 46) * mm});
            skLineSegment(sketch, "E328.MirrorCS", {"start": v(118, -50) * mm, "end": v(112, -50) * mm, "construction": true});
            skLineSegment(sketch, "E329.MirrorCS", {"start": v(240, -46) * mm, "end": v(242, -46) * mm});
            skLineSegment(sketch, "E330.MirrorCS", {"start": v(115, 42) * mm, "end": v(118.4, 42) * mm});
            skLineSegment(sketch, "E331.MirrorCS", {"start": v(110, 50) * mm, "end": v(112, 50) * mm});
            skLineSegment(sketch, "E332.MirrorCS", {"start": v(242, -50) * mm, "end": v(248, -50) * mm, "construction": true});
            skLineSegment(sketch, "E333.MirrorCS", {"start": v(150, -46) * mm, "end": v(152, -46) * mm});
            skLineSegment(sketch, "E334.MirrorCS", {"start": v(245, -42) * mm, "end": v(248.4, -42) * mm});
            skLineSegment(sketch, "E335.MirrorCS", {"start": v(112, 46) * mm, "end": v(112, 50) * mm});
            skLineSegment(sketch, "E336.MirrorCS", {"start": v(138, -50) * mm, "end": v(132, -50) * mm, "construction": true});
            skLineSegment(sketch, "E337.MirrorCS", {"start": v(138, -46) * mm, "end": v(138, -50) * mm});
            skLineSegment(sketch, "E338.MirrorCS", {"start": v(242, 50) * mm, "end": v(248, 50) * mm, "construction": true});
            skLineSegment(sketch, "E339.MirrorCS", {"start": v(111.6, 42) * mm, "end": v(110, 43.6) * mm});
            skLineSegment(sketch, "E340.MirrorCS", {"start": v(130, 43.6) * mm, "end": v(130, 46) * mm});
            skLineSegment(sketch, "E341.MirrorCS", {"start": v(230, 46) * mm, "end": v(228, 46) * mm});
            skLineSegment(sketch, "E342.MirrorCS", {"start": v(110, 43.6) * mm, "end": v(110, 46) * mm});
            skLineSegment(sketch, "E343.MirrorCS", {"start": v(131.6, 42) * mm, "end": v(130, 43.6) * mm});
            skLineSegment(sketch, "E344.MirrorCS", {"start": v(138, -50) * mm, "end": v(152, -50) * mm});
            skLineSegment(sketch, "E345.MirrorCS", {"start": v(120, -46) * mm, "end": v(118, -46) * mm});
            skLineSegment(sketch, "E346.MirrorCS", {"start": v(228.4, -42) * mm, "end": v(230, -43.6) * mm});
            skLineSegment(sketch, "E347.MirrorCS", {"start": v(225, 42) * mm, "end": v(228.4, 42) * mm});
            skLineSegment(sketch, "E348.MirrorCS", {"start": v(118, 46) * mm, "end": v(118, 50) * mm});
            skLineSegment(sketch, "E349.MirrorCS", {"start": v(110, -46) * mm, "end": v(112, -46) * mm});
            skLineSegment(sketch, "E350.MirrorCS", {"start": v(248, -46) * mm, "end": v(248, -50) * mm});
            skLineSegment(sketch, "E351.MirrorCS", {"start": v(242, 46) * mm, "end": v(242, 50) * mm});
            skLineSegment(sketch, "E352.MirrorCS", {"start": v(138, 50) * mm, "end": v(132, 50) * mm, "construction": true});
            skLineSegment(sketch, "E353.MirrorCS", {"start": v(250, 46) * mm, "end": v(248, 46) * mm});
            skLineSegment(sketch, "E354.MirrorCS", {"start": v(131.6, -42) * mm, "end": v(130, -43.6) * mm});
            skLineSegment(sketch, "E355.MirrorCS", {"start": v(118, -50) * mm, "end": v(132, -50) * mm});
            skLineSegment(sketch, "E356.MirrorCS", {"start": v(0, -50) * mm, "end": v(165, -50) * mm, "construction": true});
            skLineSegment(sketch, "E357.MirrorCS", {"start": v(165, -60) * mm, "end": v(165, -50) * mm});
            skLineSegment(sketch, "E358.MirrorCS", {"start": v(118, 50) * mm, "end": v(132, 50) * mm});
            skLineSegment(sketch, "E359.MirrorCS", {"start": v(115, -42) * mm, "end": v(111.6, -42) * mm});
            skLineSegment(sketch, "E360.MirrorCS", {"start": v(165, -50) * mm, "end": v(70, -50) * mm, "construction": true});
            skLineSegment(sketch, "E361.MirrorCS", {"start": v(242, -50) * mm, "end": v(228, -50) * mm});
            skLineSegment(sketch, "E362.MirrorCS", {"start": v(138.4, -42) * mm, "end": v(140, -43.6) * mm});
            skLineSegment(sketch, "E363.MirrorCS", {"start": v(115, -42) * mm, "end": v(118.4, -42) * mm});
            skLineSegment(sketch, "E364.MirrorCS", {"start": v(245, 42) * mm, "end": v(248.4, 42) * mm});
            skLineSegment(sketch, "E365.MirrorCS", {"start": v(138, 50) * mm, "end": v(152, 50) * mm});
            skLineSegment(sketch, "E366.MirrorCS", {"start": v(270, 5) * mm, "end": v(270, -5) * mm});
            skLineSegment(sketch, "E367.MirrorCS", {"start": v(158.4, 42) * mm, "end": v(160, 43.6) * mm});
            skLineSegment(sketch, "E368.MirrorCS", {"start": v(270, -40) * mm, "end": v(270, -50) * mm});
            skLineSegment(sketch, "E369.MirrorCS", {"start": v(260, -40) * mm, "end": v(270, -40) * mm});
            skLineSegment(sketch, "E370.MirrorCS", {"start": v(70, 50) * mm, "end": v(80, 50) * mm});
            skLineSegment(sketch, "E371.MirrorCS", {"start": v(245, 42) * mm, "end": v(241.6, 42) * mm});
            skLineSegment(sketch, "E372.MirrorCS", {"start": v(241.6, 42) * mm, "end": v(240, 43.6) * mm});
            skLineSegment(sketch, "E373.MirrorCS", {"start": v(118.4, 42) * mm, "end": v(120, 43.6) * mm});
            skLineSegment(sketch, "E374.MirrorCS", {"start": v(70, -50) * mm, "end": v(80, -50) * mm});
            skLineSegment(sketch, "E375.MirrorCS", {"start": v(241.6, -42) * mm, "end": v(240, -43.6) * mm});
            skLineSegment(sketch, "E376.MirrorCS", {"start": v(111.6, -42) * mm, "end": v(110, -43.6) * mm});
            skLineSegment(sketch, "E377.MirrorCS", {"start": v(140, -43.6) * mm, "end": v(140, -46) * mm});
            skLineSegment(sketch, "E378.MirrorCS", {"start": v(222, -50) * mm, "end": v(208, -50) * mm});
            skLineSegment(sketch, "E379.MirrorCS", {"start": v(260, -5) * mm, "end": v(270, -5) * mm});
            skLineSegment(sketch, "E380.MirrorCS", {"start": v(260, -50) * mm, "end": v(270, -50) * mm});
            skLineSegment(sketch, "E381.MirrorCS", {"start": v(120, 43.6) * mm, "end": v(120, 46) * mm});
            skLineSegment(sketch, "E382.MirrorCS", {"start": v(140, -46) * mm, "end": v(138, -46) * mm});
            skLineSegment(sketch, "E383.MirrorCS", {"start": v(242, 50) * mm, "end": v(228, 50) * mm});
            skLineSegment(sketch, "E384.MirrorCS", {"start": v(290, 50) * mm, "end": v(280, 50) * mm});
            skLineSegment(sketch, "E385.MirrorCS", {"start": v(165, 50) * mm, "end": v(70, 50) * mm, "construction": true});
            skPoint(sketch, "E386.MirrorP", {"position": v(180, -50) * mm});
            skLineSegment(sketch, "E387.MirrorCS", {"start": v(280, -50) * mm, "end": v(280, -60) * mm});
            skLineSegment(sketch, "E388.MirrorCS", {"start": v(165, -60) * mm, "end": v(180, -60) * mm});
            skLineSegment(sketch, "E389.MirrorCS", {"start": v(222, 50) * mm, "end": v(208, 50) * mm});
            skLineSegment(sketch, "E390.MirrorCS", {"start": v(165, 60) * mm, "end": v(165, 50) * mm});
            skLineSegment(sketch, "E391.MirrorCS", {"start": v(100, -50) * mm, "end": v(90, -50) * mm});
            skLineSegment(sketch, "E392.MirrorCS", {"start": v(195, -60) * mm, "end": v(180, -60) * mm});
            skLineSegment(sketch, "E393.MirrorCS", {"start": v(100, -40) * mm, "end": v(100, -50) * mm});
            skLineSegment(sketch, "E394.MirrorCS", {"start": v(250, -60) * mm, "end": v(250, -50) * mm});
            skLineSegment(sketch, "E395.MirrorCS", {"start": v(100, 5) * mm, "end": v(100, -5) * mm});
            skLineSegment(sketch, "E396.MirrorCS", {"start": v(260, -40) * mm, "end": v(260, -50) * mm});
            skLineSegment(sketch, "E397.MirrorCS", {"start": v(70, 50) * mm, "end": v(0, 50) * mm});
            skPoint(sketch, "E398.MirrorP", {"position": v(265, 0) * mm});
            skLineSegment(sketch, "E399.MirrorCS", {"start": v(90, -40) * mm, "end": v(90, -50) * mm});
            skLineSegment(sketch, "E400.MirrorCS", {"start": v(260, 40) * mm, "end": v(270, 40) * mm});
            skLineSegment(sketch, "E401.MirrorCS", {"start": v(100, -40) * mm, "end": v(90, -40) * mm});
            skLineSegment(sketch, "E402.MirrorCS", {"start": v(195, -50) * mm, "end": v(290, -50) * mm, "construction": true});
            skLineSegment(sketch, "E403.MirrorCS", {"start": v(270, 40) * mm, "end": v(270, 50) * mm});
            skLineSegment(sketch, "E404.MirrorCS", {"start": v(280, -60) * mm, "end": v(250, -60) * mm});
            skLineSegment(sketch, "E405.MirrorCS", {"start": v(260, 50) * mm, "end": v(270, 50) * mm});
            skPoint(sketch, "E406.MirrorP", {"position": v(180, 50) * mm});
            skLineSegment(sketch, "E407.MirrorCS", {"start": v(90, 5) * mm, "end": v(90, -5) * mm});
            skLineSegment(sketch, "E408.MirrorCS", {"start": v(195, -60) * mm, "end": v(195, -50) * mm});
            skLineSegment(sketch, "E409.MirrorCS", {"start": v(195, 60) * mm, "end": v(180, 60) * mm});
            skLineSegment(sketch, "E410.MirrorCS", {"start": v(260, 5) * mm, "end": v(260, -5) * mm});
            skLineSegment(sketch, "E411.MirrorCS", {"start": v(260, 5) * mm, "end": v(270, 5) * mm});
            skLineSegment(sketch, "E412.MirrorCS", {"start": v(100, 50) * mm, "end": v(90, 50) * mm});
            skLineSegment(sketch, "E413.MirrorCS", {"start": v(208.4, -42) * mm, "end": v(228.4, -42) * mm, "construction": true});
            skLineSegment(sketch, "E414.MirrorCS", {"start": v(165, 60) * mm, "end": v(180, 60) * mm});
            skLineSegment(sketch, "E415.MirrorCS", {"start": v(90, 40) * mm, "end": v(90, 50) * mm});
            skLineSegment(sketch, "E416.MirrorCS", {"start": v(280, 50) * mm, "end": v(280, 60) * mm});
            skLineSegment(sketch, "E417.MirrorCS", {"start": v(110, -60) * mm, "end": v(110, -50) * mm});
            skLineSegment(sketch, "E418.MirrorCS", {"start": v(100, -5) * mm, "end": v(90, -5) * mm});
            skLineSegment(sketch, "E419.MirrorCS", {"start": v(195, 50) * mm, "end": v(290, 50) * mm, "construction": true});
            skLineSegment(sketch, "E420.MirrorCS", {"start": v(100, 40) * mm, "end": v(100, 50) * mm});
            skLineSegment(sketch, "E421.MirrorCS", {"start": v(110, 60) * mm, "end": v(110, 50) * mm});
            skLineSegment(sketch, "E422.MirrorCS", {"start": v(100, 40) * mm, "end": v(90, 40) * mm});
            skLineSegment(sketch, "E423.MirrorCS", {"start": v(280, 60) * mm, "end": v(250, 60) * mm});
            skLineSegment(sketch, "E424.MirrorCS", {"start": v(151.6, 42) * mm, "end": v(131.6, 42) * mm, "construction": true});
            skPoint(sketch, "E425.MirrorP", {"position": v(265, -45) * mm});
            skLineSegment(sketch, "E426.MirrorCS", {"start": v(151.6, -42) * mm, "end": v(131.6, -42) * mm, "construction": true});
            skPoint(sketch, "E427.MirrorP", {"position": v(265, 45) * mm});
            skLineSegment(sketch, "E428.MirrorCS", {"start": v(195, 60) * mm, "end": v(195, 50) * mm});
            skLineSegment(sketch, "E429.MirrorCS", {"start": v(0, 0) * mm, "end": v(290, 0) * mm, "construction": true});
            skLineSegment(sketch, "E430.MirrorCS", {"start": v(80, -60) * mm, "end": v(110, -60) * mm});
            skLineSegment(sketch, "E431.MirrorCS", {"start": v(180, 63.21) * mm, "end": v(180, -50) * mm, "construction": true});
            skLineSegment(sketch, "E432.MirrorCS", {"start": v(250, 60) * mm, "end": v(250, 50) * mm});
            skLineSegment(sketch, "E433.MirrorCS", {"start": v(265, 50) * mm, "end": v(265, -50) * mm, "construction": true});
            skLineSegment(sketch, "E434.MirrorCS", {"start": v(208.4, 42) * mm, "end": v(228.4, 42) * mm, "construction": true});
            skLineSegment(sketch, "E435.MirrorCS", {"start": v(80, 60) * mm, "end": v(110, 60) * mm});
            skLineSegment(sketch, "E436.MirrorCS", {"start": v(0, -50) * mm, "end": v(290, -50) * mm, "construction": true});
            skLineSegment(sketch, "E437.MirrorCS", {"start": v(260, 40) * mm, "end": v(260, 50) * mm});
            skLineSegment(sketch, "E438.MirrorCS", {"start": v(290, -50) * mm, "end": v(290, 50) * mm});
            skLineSegment(sketch, "E439.MirrorCS", {"start": v(0, 50) * mm, "end": v(165, 50) * mm, "construction": true});
            skLineSegment(sketch, "E440.MirrorCS", {"start": v(80, -50) * mm, "end": v(80, -60) * mm});
            skLineSegment(sketch, "E441.MirrorCS", {"start": v(80, 50) * mm, "end": v(80, 60) * mm});
            skLineSegment(sketch, "E442.MirrorCS", {"start": v(100, 5) * mm, "end": v(90, 5) * mm});
            skLineSegment(sketch, "E443.bottom", {"start": v(55, 40) * mm, "end": v(-55, 40) * mm});
            skLineSegment(sketch, "E443.top", {"start": v(55, 20) * mm, "end": v(-55, 20) * mm});
            skLineSegment(sketch, "E443.left", {"start": v(60, 35) * mm, "end": v(60, 25) * mm});
            skLineSegment(sketch, "E443.right", {"start": v(-60, 35) * mm, "end": v(-60, 25) * mm});
            skPoint(sketch, "E443.middle", {"position": v(0, 30) * mm});
            skPoint(sketch, "E444.visualSharp", {"position": v(-60, 40) * mm});
            skArc(sketch, "E444.filletArc", {"start": v(-55, 40) * mm, "mid": v(-58.54, 38.54) * mm, "end": v(-60, 35) * mm});
            skPoint(sketch, "E445.visualSharp", {"position": v(-60, 20) * mm});
            skArc(sketch, "E445.filletArc", {"start": v(-60, 25) * mm, "mid": v(-58.54, 21.46) * mm, "end": v(-55, 20) * mm});
            skPoint(sketch, "E446.visualSharp", {"position": v(60, 20) * mm});
            skArc(sketch, "E446.filletArc", {"start": v(55, 20) * mm, "mid": v(58.54, 21.46) * mm, "end": v(60, 25) * mm});
            skPoint(sketch, "E447.visualSharp", {"position": v(60, 40) * mm});
            skArc(sketch, "E447.filletArc", {"start": v(60, 35) * mm, "mid": v(58.54, 38.54) * mm, "end": v(55, 40) * mm});
            skCircle(sketch, "E448", {"center": v(-265, 30) * mm, "radius": 2.75 * mm});
            skCircle(sketch, "E449", {"center": v(-265, 15) * mm, "radius": 2.75 * mm});
            skCircle(sketch, "E450.MirrorC", {"center": v(-265, -15) * mm, "radius": 2.75 * mm});
            skCircle(sketch, "E451.MirrorC", {"center": v(-265, -30) * mm, "radius": 2.75 * mm});
            skCircle(sketch, "E452.MirrorC", {"center": v(-95, 30) * mm, "radius": 2.75 * mm});
            skCircle(sketch, "E453.MirrorC", {"center": v(-95, 15) * mm, "radius": 2.75 * mm});
            skCircle(sketch, "E454.MirrorC", {"center": v(-95, -30) * mm, "radius": 2.75 * mm});
            skCircle(sketch, "E455.MirrorC", {"center": v(-95, -15) * mm, "radius": 2.75 * mm});
            skCircle(sketch, "E456.MirrorC", {"center": v(95, 30) * mm, "radius": 2.75 * mm});
            skCircle(sketch, "E457.MirrorC", {"center": v(95, 15) * mm, "radius": 2.75 * mm});
            skCircle(sketch, "E458.MirrorC", {"center": v(95, -30) * mm, "radius": 2.75 * mm});
            skCircle(sketch, "E459.MirrorC", {"center": v(95, -15) * mm, "radius": 2.75 * mm});
            skCircle(sketch, "E460.MirrorC", {"center": v(265, -30) * mm, "radius": 2.75 * mm});
            skCircle(sketch, "E461.MirrorC", {"center": v(265, -15) * mm, "radius": 2.75 * mm});
            skCircle(sketch, "E462.MirrorC", {"center": v(265, 30) * mm, "radius": 2.75 * mm});
            skCircle(sketch, "E463.MirrorC", {"center": v(265, 15) * mm, "radius": 2.75 * mm});
            skLineSegment(sketch, "E464.bottom", {"start": v(-135, 20) * mm, "end": v(-225, 20) * mm});
            skLineSegment(sketch, "E464.top", {"start": v(-135, -20) * mm, "end": v(-225, -20) * mm});
            skLineSegment(sketch, "E464.left", {"start": v(-130, 15) * mm, "end": v(-130, -15) * mm});
            skLineSegment(sketch, "E464.right", {"start": v(-230, 15) * mm, "end": v(-230, -15) * mm});
            skPoint(sketch, "E464.middle", {"position": v(-180, 0) * mm});
            skPoint(sketch, "E465.visualSharp", {"position": v(-230, 20) * mm});
            skArc(sketch, "E465.filletArc", {"start": v(-225, 20) * mm, "mid": v(-228.54, 18.54) * mm, "end": v(-230, 15) * mm});
            skPoint(sketch, "E466.visualSharp", {"position": v(-230, -20) * mm});
            skArc(sketch, "E466.filletArc", {"start": v(-230, -15) * mm, "mid": v(-228.54, -18.54) * mm, "end": v(-225, -20) * mm});
            skPoint(sketch, "E467.visualSharp", {"position": v(-130, -20) * mm});
            skArc(sketch, "E467.filletArc", {"start": v(-135, -20) * mm, "mid": v(-131.46, -18.54) * mm, "end": v(-130, -15) * mm});
            skPoint(sketch, "E468.visualSharp", {"position": v(-130, 20) * mm});
            skArc(sketch, "E468.filletArc", {"start": v(-130, 15) * mm, "mid": v(-131.46, 18.54) * mm, "end": v(-135, 20) * mm});
            skArc(sketch, "E469.MirrorCS", {"start": v(130, 15) * mm, "mid": v(131.46, 18.54) * mm, "end": v(135, 20) * mm});
            skArc(sketch, "E470.MirrorCS", {"start": v(225, 20) * mm, "mid": v(228.54, 18.54) * mm, "end": v(230, 15) * mm});
            skArc(sketch, "E471.MirrorCS", {"start": v(230, -15) * mm, "mid": v(228.54, -18.54) * mm, "end": v(225, -20) * mm});
            skArc(sketch, "E472.MirrorCS", {"start": v(135, -20) * mm, "mid": v(131.46, -18.54) * mm, "end": v(130, -15) * mm});
            skPoint(sketch, "E473.MirrorP", {"position": v(130, -20) * mm});
            skPoint(sketch, "E474.MirrorP", {"position": v(230, -20) * mm});
            skPoint(sketch, "E475.MirrorP", {"position": v(180, 0) * mm});
            skLineSegment(sketch, "E476.MirrorCS", {"start": v(230, 15) * mm, "end": v(230, -15) * mm});
            skLineSegment(sketch, "E477.MirrorCS", {"start": v(135, 20) * mm, "end": v(225, 20) * mm});
            skLineSegment(sketch, "E478.MirrorCS", {"start": v(135, -20) * mm, "end": v(225, -20) * mm});
            skPoint(sketch, "E479.MirrorP", {"position": v(130, 20) * mm});
            skLineSegment(sketch, "E480.MirrorCS", {"start": v(130, 15) * mm, "end": v(130, -15) * mm});
            skPoint(sketch, "E481.MirrorP", {"position": v(230, 20) * mm});
            skSolve(sketch);
        }
        {
            var Q0;
            Q0=makeQuery(id+"F0.imprint","IMPRINT",FACE,{"disambiguationData":[TD([[makeQuery(id+"F0.imprint","IMPRINT",EDGE,{"derivedFrom":sQuery(id+"F0.wireOp",EDGE,"E0.right")}),-1.0]])]});
            extrude(context, id + "F1", {"entities" : qUnion([Q0]), "depth" : 10 * mm, "offsetDistance" : 25 * mm});
        }
    });
